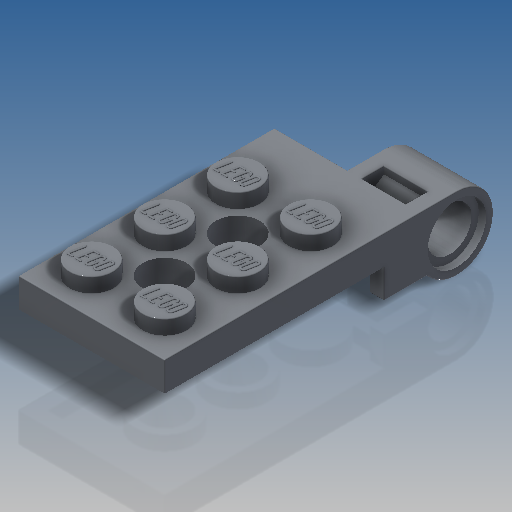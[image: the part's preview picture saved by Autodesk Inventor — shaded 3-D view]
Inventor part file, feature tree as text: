
AUTODESK INVENTOR PART (.ipt)
format: ipt  version: 2019.4 (Build 234330000, 330)  size: 2,011,648 bytes
history: native  units: in
note: dims shown in document units (in); Inventor stores cm internally (conversion verified against a paired STEP export)
features: sketch x10, extrude x7, other x6, plane x1, fillet x1
ambient origin geometry x8: Origin, YZ Plane, XZ Plane, XY Plane, X Axis, Y Axis, Z Axis, Center Point
bodies: Solid1 (feature_tree)
feature tree (25):
  sketch  "Sketch2"  dims[d0=0.6299in d1=1.1024in]
  extrude  "Extrusion1"  Depth=1.1024in
  extrude  "Extrusion2"  Depth=0.063in
  extrude  "Extrusion3"  Depth=0.189in
  plane  "Work Plane1"
  sketch  "Sketch4"  dims[d4=0.189in d5=0.2564in]
  extrude  "Extrusion4"  Depth=0.126in
  extrude  "Extrusion5"  Depth=0.063in
  extrude  "Extrusion6"  Depth=0.1575in
  extrude  "Extrusion7"  Depth=0.1575in
  other  "LEGO:1"
  other  "LEGO:2"
  other  "LEGO:3"
  other  "LEGO:4"
  other  "LEGO:5"
  other  "LEGO:6"
  fillet  "Fillet1"  Radius=0.063in
  sketch  "Sketch3"  dims[d2=0.063in d3=0.063in]
  sketch  "Sketch5"  dims[d6=0.315in d7=0.126in]
  sketch  "Sketch6"  dims[d8=0.0in d9=0.063in]
  sketch  "Sketch7"  dims[d10=0.0in d11=0.1575in]
  sketch  "Sketch8"  dims[d12=0.315in d13=0.1575in d14=0.063in]
  sketch  "Sketch9"  dims[d15=0.0in]
  sketch  "Sketch10"  dims[d16=0.1575in]
  sketch  "Sketch11"  dims[d17=0.252in d18=0.189in d19=0.0945in d20=0.0315in d21=0.0945in d22=0.315in d23=0.0in d24=0.252in d25=0.0in d26=0.189in d27=0.0in d28=0.315in d29=0.189in d30=0.063in d31=0.0in d32=0.0039in d33=0.0in d34=0.0in d35=0.0in d36=0.0in d37=0.0in d38=0.0in d39=0.0in d40=0.0in d41=0.0in d42=0.0079in d43=0.0732in d44=0.0281in d45=0.035in d46=0.0079in d47=0.0139in d48=0.0281in d49=0.035in d50=0.0281in d51=0.0159in d52=0.0177in d53=0.035in d54=0.5428in d55=0.0079in d56=0.0732in d57=0.0281in d58=0.035in d59=0.0079in d60=0.0139in d61=0.0281in d62=0.035in d63=0.0281in d64=0.0159in d65=0.0177in d66=0.035in d67=0.5428in d68=0.0079in d69=0.0732in d70=0.0281in d71=0.035in d72=0.0079in d73=0.0139in d74=0.0281in d75=0.035in d76=0.0281in d77=0.0159in d78=0.0177in d79=0.035in d80=0.5428in d81=0.0079in d82=0.0732in d83=0.0281in d84=0.035in d85=0.0079in d86=0.0139in d87=0.0281in d88=0.035in d89=0.0281in d90=0.0159in d91=0.0177in d92=0.035in d93=0.5428in d94=0.0079in d95=0.0732in d96=0.0281in d97=0.035in d98=0.0079in d99=0.0139in d100=0.0281in d101=0.035in d102=0.0281in d103=0.0159in d104=0.0177in d105=0.035in d106=0.5428in d107=0.0079in d108=0.0732in d109=0.0281in d110=0.035in d111=0.0079in d112=0.0139in d113=0.0281in d114=0.035in d115=0.0281in d116=0.0159in d117=0.0177in d118=0.035in d119=0.5428in]
